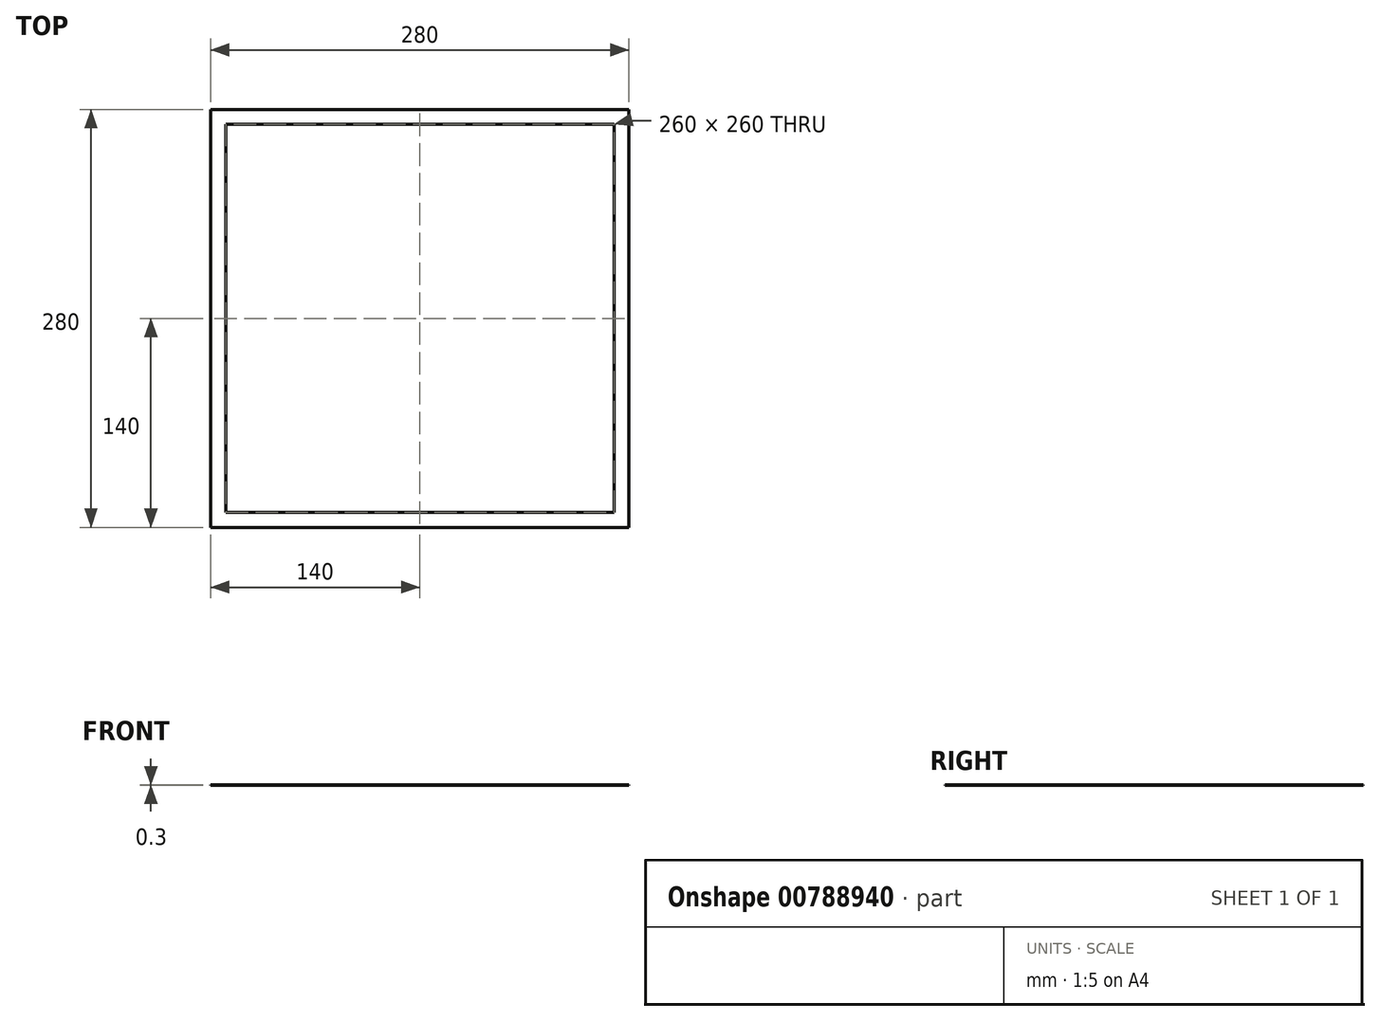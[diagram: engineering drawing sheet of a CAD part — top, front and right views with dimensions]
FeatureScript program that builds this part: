
annotation { "Feature Type Name" : "Feature", "Feature Type Description" : "" }
export const myFeature = defineFeature(function(context is Context, id is Id, definition is map)
    precondition{}
    {
        {
            var Q0;
            Q0=qCreatedBy(makeId("Top.planeOp"),FACE);
            var sketch = newSketch(context, id + "F0", { "sketchPlane" : qUnion([Q0])});
            skLineSegment(sketch, "E0.bottom", {"start": v(140, -140) * mm, "end": v(-140, -140) * mm});
            skLineSegment(sketch, "E0.top", {"start": v(140, 140) * mm, "end": v(-140, 140) * mm});
            skLineSegment(sketch, "E0.left", {"start": v(140, -140) * mm, "end": v(140, 140) * mm});
            skLineSegment(sketch, "E0.right", {"start": v(-140, -140) * mm, "end": v(-140, 140) * mm});
            skPoint(sketch, "E0.middle", {"position": v(0, 0) * mm});
            skLineSegment(sketch, "E1.bottom", {"start": v(130, -130) * mm, "end": v(-130, -130) * mm});
            skLineSegment(sketch, "E1.top", {"start": v(130, 130) * mm, "end": v(-130, 130) * mm});
            skLineSegment(sketch, "E1.left", {"start": v(130, -130) * mm, "end": v(130, 130) * mm});
            skLineSegment(sketch, "E1.right", {"start": v(-130, -130) * mm, "end": v(-130, 130) * mm});
            skSolve(sketch);
        }
        {
            var Q0;
            Q0=makeQuery(id+"F0.imprint","IMPRINT",FACE,{"disambiguationData":[TD([[makeQuery(id+"F0.imprint","IMPRINT",EDGE,{"derivedFrom":sQuery(id+"F0.wireOp",EDGE,"E0.bottom")}),-1.0]])]});
            extrude(context, id + "F1", {"entities" : qUnion([Q0]), "depth" : .3 * mm, "offsetDistance" : 25.4 * mm});
        }
    });
